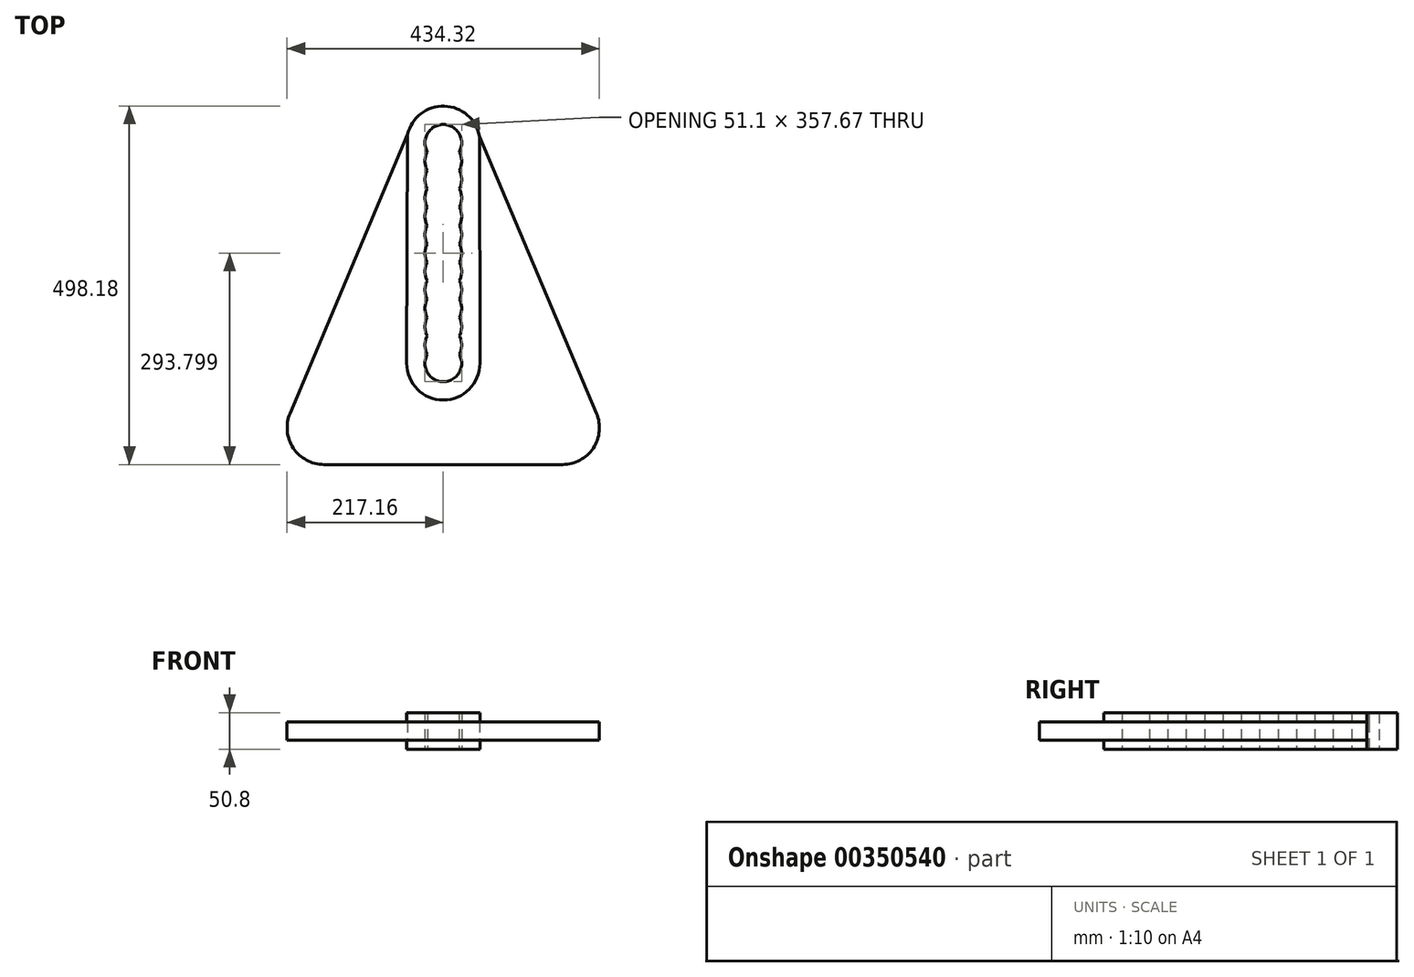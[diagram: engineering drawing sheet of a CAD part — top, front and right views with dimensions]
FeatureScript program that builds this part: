
annotation { "Feature Type Name" : "Feature", "Feature Type Description" : "" }
export const myFeature = defineFeature(function(context is Context, id is Id, definition is map)
    precondition{}
    {
        {
            var Q0;
            Q0=qCreatedBy(makeId("Top.planeOp"),FACE);
            var sketch = newSketch(context, id + "F0", { "sketchPlane" : qUnion([Q0])});
            skLineSegment(sketch, "E0.top", {"start": v(166.06, -249.1) * mm, "end": v(-166.06, -249.1) * mm});
            skPoint(sketch, "E0.middle", {"position": v(0, 0) * mm});
            skArc(sketch, "E1", {"start": v(-22.13, -95.8) * mm, "mid": v(0, -134.13) * mm, "end": v(22.13, -95.8) * mm});
            skArc(sketch, "E2.0.1.0", {"start": v(22.13, -95.8) * mm, "mid": v(25.55, -83.03) * mm, "end": v(22.13, -70.26) * mm});
            skArc(sketch, "E2.0.2.0", {"start": v(22.13, -70.26) * mm, "mid": v(25.55, -57.48) * mm, "end": v(22.13, -44.7) * mm});
            skArc(sketch, "E2.0.3.0", {"start": v(22.13, -44.7) * mm, "mid": v(25.55, -31.93) * mm, "end": v(22.13, -19.16) * mm});
            skArc(sketch, "E2.0.4.0", {"start": v(22.13, -19.16) * mm, "mid": v(25.55, -6.39) * mm, "end": v(22.13, 6.39) * mm});
            skArc(sketch, "E2.0.5.0", {"start": v(22.13, 6.39) * mm, "mid": v(25.55, 19.16) * mm, "end": v(22.13, 31.93) * mm});
            skArc(sketch, "E2.0.6.0", {"start": v(22.13, 31.93) * mm, "mid": v(25.55, 44.7) * mm, "end": v(22.13, 57.48) * mm});
            skArc(sketch, "E2.0.7.0", {"start": v(22.13, 57.48) * mm, "mid": v(25.55, 70.26) * mm, "end": v(22.13, 83.03) * mm});
            skArc(sketch, "E2.0.8.0", {"start": v(22.13, 83.03) * mm, "mid": v(25.55, 95.8) * mm, "end": v(22.13, 108.58) * mm});
            skArc(sketch, "E2.0.9.0", {"start": v(22.13, 108.58) * mm, "mid": v(25.55, 121.35) * mm, "end": v(22.13, 134.13) * mm});
            skArc(sketch, "E2.0.10.0", {"start": v(22.13, 134.13) * mm, "mid": v(25.55, 146.9) * mm, "end": v(22.13, 159.67) * mm});
            skArc(sketch, "E2.0.11.0", {"start": v(22.13, 159.67) * mm, "mid": v(25.55, 172.45) * mm, "end": v(22.13, 185.22) * mm});
            skArc(sketch, "E3.0.0.12", {"start": v(22.13, 185.22) * mm, "mid": v(0, 223.54) * mm, "end": v(-22.13, 185.22) * mm});
            skArc(sketch, "E4", {"start": v(-213.15, -178.16) * mm, "mid": v(-208.63, -226.25) * mm, "end": v(-166.06, -249.1) * mm});
            skArc(sketch, "E5.MirrorC", {"start": v(213.12, -178.1) * mm, "mid": v(208.65, -226.22) * mm, "end": v(166.06, -249.1) * mm});
            skArc(sketch, "E6", {"start": v(50.34, 206.76) * mm, "mid": v(1.49, 249.07) * mm, "end": v(-49.74, 209.67) * mm});
            skLineSegment(sketch, "E7", {"start": v(-49.74, 209.67) * mm, "end": v(-213.15, -178.16) * mm});
            skLineSegment(sketch, "E8", {"start": v(50.34, 206.76) * mm, "end": v(213.12, -178.1) * mm});
            skPoint(sketch, "E9.orphan", {"position": v(217.16, 249.1) * mm});
            skPoint(sketch, "E10.orphan", {"position": v(-217.16, 249.1) * mm});
            skPoint(sketch, "E11.orphan", {"position": v(-217.16, -249.1) * mm});
            skPoint(sketch, "E12.orphan", {"position": v(217.16, -249.1) * mm});
            skPoint(sketch, "E13.orphan", {"position": v(0, -249.1) * mm});
            skArc(sketch, "E14.trimOffspring", {"start": v(-22.13, -70.26) * mm, "mid": v(-25.55, -83.03) * mm, "end": v(-22.13, -95.8) * mm});
            skArc(sketch, "E15.trimOffspring", {"start": v(-22.13, -44.7) * mm, "mid": v(-25.55, -57.48) * mm, "end": v(-22.13, -70.26) * mm});
            skArc(sketch, "E16.trimOffspring", {"start": v(-22.13, -19.16) * mm, "mid": v(-25.55, -31.93) * mm, "end": v(-22.13, -44.7) * mm});
            skArc(sketch, "E17.trimOffspring", {"start": v(-22.13, 6.39) * mm, "mid": v(-25.55, -6.39) * mm, "end": v(-22.13, -19.16) * mm});
            skArc(sketch, "E18.trimOffspring", {"start": v(-22.13, 31.93) * mm, "mid": v(-25.55, 19.16) * mm, "end": v(-22.13, 6.39) * mm});
            skArc(sketch, "E19.trimOffspring", {"start": v(-22.13, 57.48) * mm, "mid": v(-25.55, 44.7) * mm, "end": v(-22.13, 31.93) * mm});
            skArc(sketch, "E20.trimOffspring", {"start": v(-22.13, 83.03) * mm, "mid": v(-25.55, 70.26) * mm, "end": v(-22.13, 57.48) * mm});
            skArc(sketch, "E21.trimOffspring", {"start": v(-22.13, 108.58) * mm, "mid": v(-25.55, 95.8) * mm, "end": v(-22.13, 83.03) * mm});
            skArc(sketch, "E22.trimOffspring", {"start": v(-22.13, 134.13) * mm, "mid": v(-25.55, 121.35) * mm, "end": v(-22.13, 108.58) * mm});
            skArc(sketch, "E23.trimOffspring", {"start": v(-22.13, 159.67) * mm, "mid": v(-25.55, 146.9) * mm, "end": v(-22.13, 134.13) * mm});
            skArc(sketch, "E24.trimOffspring", {"start": v(-22.13, 185.22) * mm, "mid": v(-25.55, 172.45) * mm, "end": v(-22.13, 159.67) * mm});
            skPoint(sketch, "E25.start.orphan", {"position": v(0, 249.1) * mm});
            skLineSegment(sketch, "E26", {"start": v(0, 198) * mm, "end": v(25.55, 198) * mm});
            skLineSegment(sketch, "E27", {"start": v(25.55, 198) * mm, "end": v(0, 198) * mm});
            skLineSegment(sketch, "E28", {"start": v(0, 198) * mm, "end": v(-25.55, 198) * mm});
            skArc(sketch, "E29.0", {"start": v(-50.95, -108.58) * mm, "mid": v(0, -159.53) * mm, "end": v(50.95, -108.58) * mm});
            skLineSegment(sketch, "E30", {"start": v(50.34, 206.76) * mm, "end": v(50.95, -108.58) * mm});
            skLineSegment(sketch, "E31", {"start": v(-49.74, 209.67) * mm, "end": v(-50.95, -108.58) * mm});
            skSolve(sketch);
        }
        {
            var Q0;
            Q0=makeQuery(id+"F0.imprint","IMPRINT",FACE,{"disambiguationData":[TD([[makeQuery(id+"F0.imprint","IMPRINT",EDGE,{"derivedFrom":sQuery(id+"F0.wireOp",EDGE,"E1")}),-1.0]])]});
            extrude(context, id + "F1", {"entities" : qUnion([Q0]), "endBound" : BoundingType.SYMMETRIC, "depth" : 50.8 * mm});
        }
        {
            var Q0;
            Q0=makeQuery(id+"F0.imprint","IMPRINT",FACE,{"disambiguationData":[TD([[makeQuery(id+"F0.imprint","IMPRINT",EDGE,{"derivedFrom":sQuery(id+"F0.wireOp",EDGE,"E0.top")}),-1.0]])]});
            extrude(context, id + "F2", {"entities" : qUnion([Q0]), "operationType" : NewBodyOperationType.ADD, "endBound" : BoundingType.SYMMETRIC, "depth" : 25.4 * mm});
        }
    });
